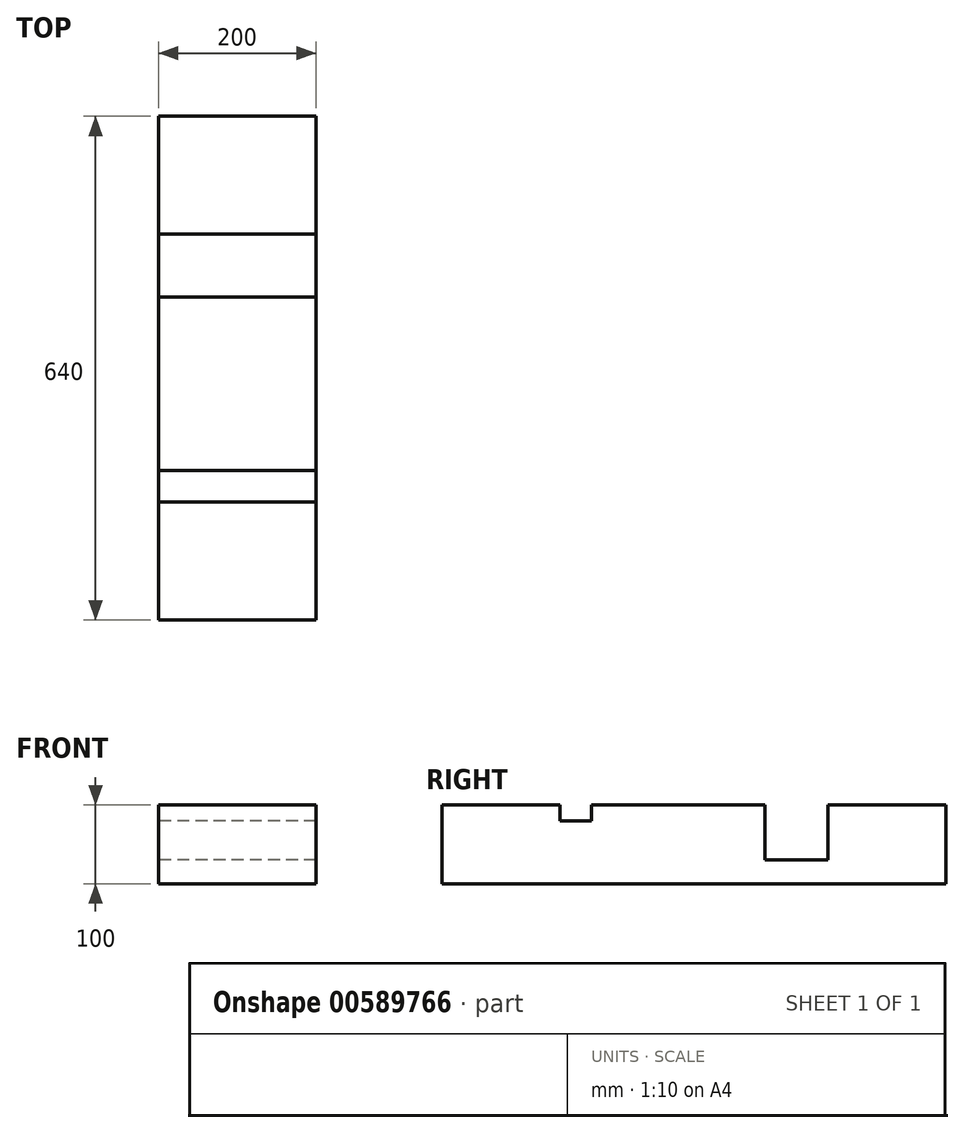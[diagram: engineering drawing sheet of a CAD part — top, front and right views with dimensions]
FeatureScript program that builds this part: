
annotation { "Feature Type Name" : "Feature", "Feature Type Description" : "" }
export const myFeature = defineFeature(function(context is Context, id is Id, definition is map)
    precondition{}
    {
        {
            var Q0;
            Q0=qCreatedBy(makeId("Right.planeOp"),FACE);
            var sketch = newSketch(context, id + "F0", { "sketchPlane" : qUnion([Q0])});
            skLineSegment(sketch, "E0.bottom", {"start": v(-320, 50) * mm, "end": v(-170, 50) * mm});
            skLineSegment(sketch, "E0.top", {"start": v(-320, -50) * mm, "end": v(320, -50) * mm});
            skLineSegment(sketch, "E0.left", {"start": v(-320, 50) * mm, "end": v(-320, -50) * mm});
            skLineSegment(sketch, "E0.right", {"start": v(320, 50) * mm, "end": v(320, -50) * mm});
            skPoint(sketch, "E0.middle", {"position": v(0, 0) * mm});
            skLineSegment(sketch, "E1", {"start": v(320, 50) * mm, "end": v(170, 50) * mm});
            skLineSegment(sketch, "E2", {"start": v(170, 50) * mm, "end": v(170, -50) * mm});
            skLineSegment(sketch, "E3", {"start": v(170, -50) * mm, "end": v(130, -50) * mm});
            skLineSegment(sketch, "E4", {"start": v(130, -50) * mm, "end": v(130, -20) * mm});
            skLineSegment(sketch, "E5", {"start": v(90, 50) * mm, "end": v(90, -50) * mm});
            skLineSegment(sketch, "E6", {"start": v(90, 50) * mm, "end": v(-130, 50) * mm});
            skLineSegment(sketch, "E7", {"start": v(-130, 50) * mm, "end": v(-130, 30) * mm});
            skLineSegment(sketch, "E8", {"start": v(-130, 30) * mm, "end": v(-170, 30) * mm});
            skLineSegment(sketch, "E9", {"start": v(-170, 30) * mm, "end": v(-170, 50) * mm});
            skLineSegment(sketch, "E10", {"start": v(90, -50) * mm, "end": v(90, -20) * mm});
            skLineSegment(sketch, "E11", {"start": v(90, -20) * mm, "end": v(130, -20) * mm});
            skLineSegment(sketch, "E12.trimOffspring", {"start": v(-130, 50) * mm, "end": v(90, 50) * mm});
            skLineSegment(sketch, "E13", {"start": v(130, -20) * mm, "end": v(170, -20) * mm});
            skLineSegment(sketch, "E14.trimOffspring", {"start": v(170, 50) * mm, "end": v(320, 50) * mm});
            skSolve(sketch);
        }
        {
            var Q0;
            Q0 = qSketchRegion(id + "F0", true);
            extrude(context, id + "F1", {"entities" : qUnion([Q0]), "endBound" : BoundingType.SYMMETRIC, "depth" : 200 * mm, "offsetDistance" : 25 * mm});
        }
    });
